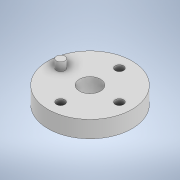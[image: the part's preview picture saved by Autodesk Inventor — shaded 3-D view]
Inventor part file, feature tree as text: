
AUTODESK INVENTOR PART (.ipt)
format: ipt  version: 2020.3 (Build 243373000, 373)  size: 115,200 bytes
history: native  units: mm
features: extrude x2, sketch x1
ambient origin geometry x8: Origin, YZ Plane, XZ Plane, XY Plane, X Axis, Y Axis, Z Axis, Center Point
bodies: Solid1 (feature_tree)
feature tree (3):
  sketch  "Sketch1"  dims[d0=14.0mm d1=2.0mm d2=40.0mm d4=360.0deg d6=3.0mm d7=5.0mm d8=4.0mm d9=0.0mm d10=6.0mm d11=0.0mm]
  extrude  "Extrusion1"  Depth=2.0mm
  extrude  "Extrusion2"  Depth=6.0mm TaperAngle=360.0deg
